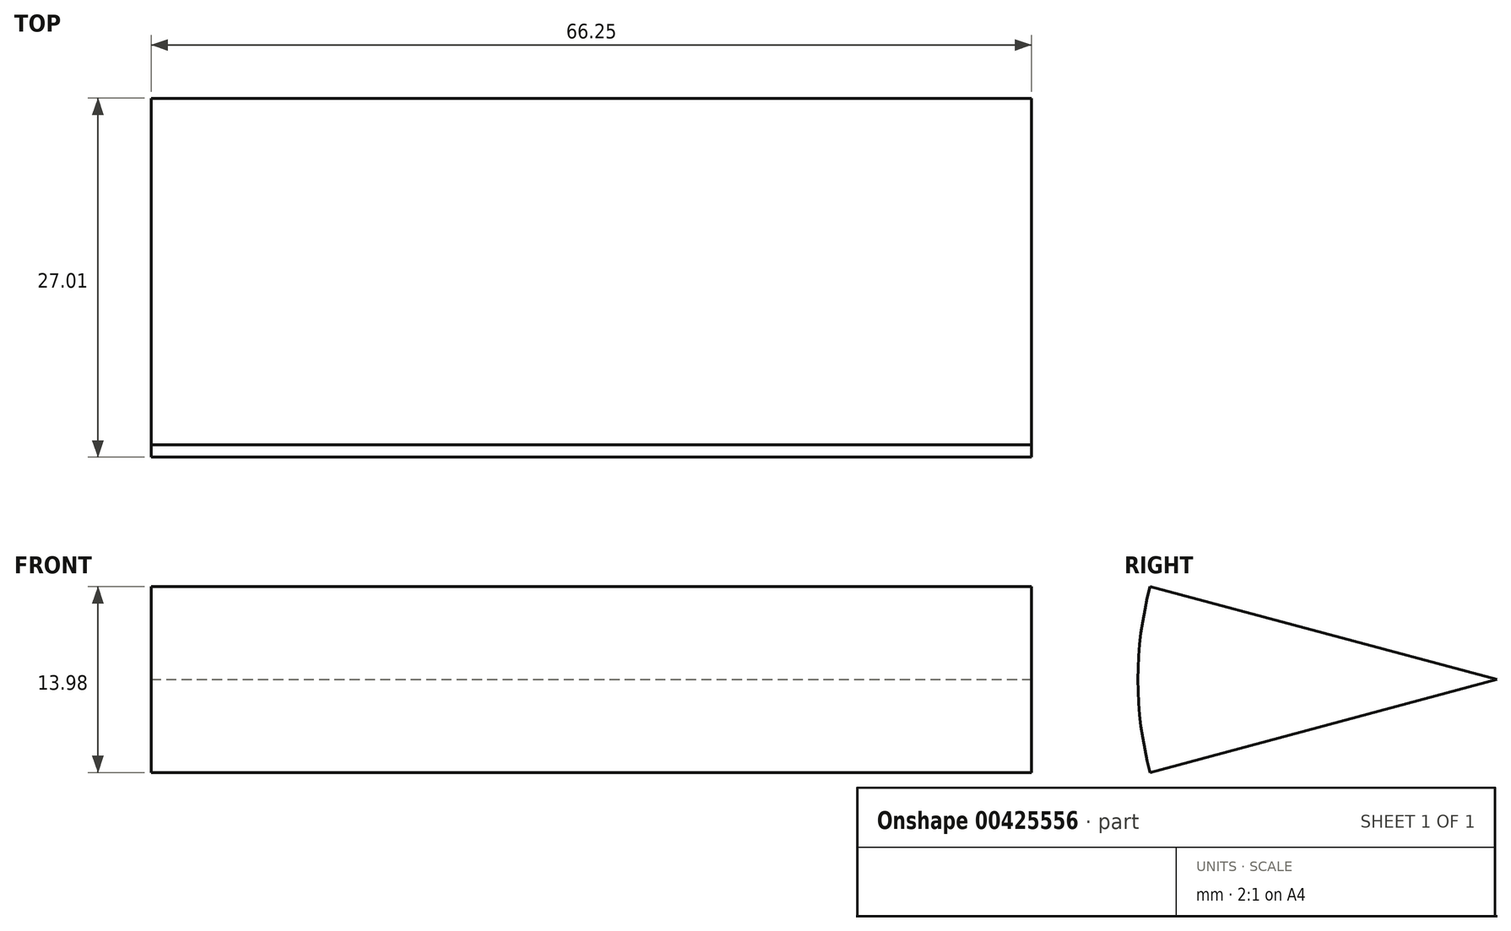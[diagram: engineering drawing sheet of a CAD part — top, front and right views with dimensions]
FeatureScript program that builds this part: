
annotation { "Feature Type Name" : "Feature", "Feature Type Description" : "" }
export const myFeature = defineFeature(function(context is Context, id is Id, definition is map)
    precondition{}
    {
        {
            var Q0;
            Q0=qCreatedBy(makeId("Top.planeOp"),FACE);
            var sketch = newSketch(context, id + "F0", { "sketchPlane" : qUnion([Q0])});
            skLineSegment(sketch, "E0.bottom", {"start": v(-51.54, -42.35) * mm, "end": v(14.71, -42.35) * mm});
            skLineSegment(sketch, "E0.top", {"start": v(-51.54, -69.36) * mm, "end": v(14.71, -69.36) * mm});
            skLineSegment(sketch, "E0.left", {"start": v(-51.54, -42.35) * mm, "end": v(-51.54, -69.36) * mm});
            skLineSegment(sketch, "E0.right", {"start": v(14.71, -42.35) * mm, "end": v(14.71, -69.36) * mm});
            skSolve(sketch);
        }
        {
            var Q0;
            Q0=makeQuery(id+"F0.imprint","IMPRINT",FACE,{"disambiguationData":[TD([[makeQuery(id+"F0.imprint","IMPRINT",EDGE,{"derivedFrom":sQuery(id+"F0.wireOp",EDGE,"E0.bottom")}),-1.0]])]});
            var Q1;
            Q1=sQuery(id+"F0.wireOp",EDGE,"E0.bottom");
            revolve(context, id + "F1", {"entities" : qUnion([Q0]), "axis" : qUnion([Q1]), "revolveType" : RevolveType.SYMMETRIC, "angle" : 30 * degree});
        }
    });
